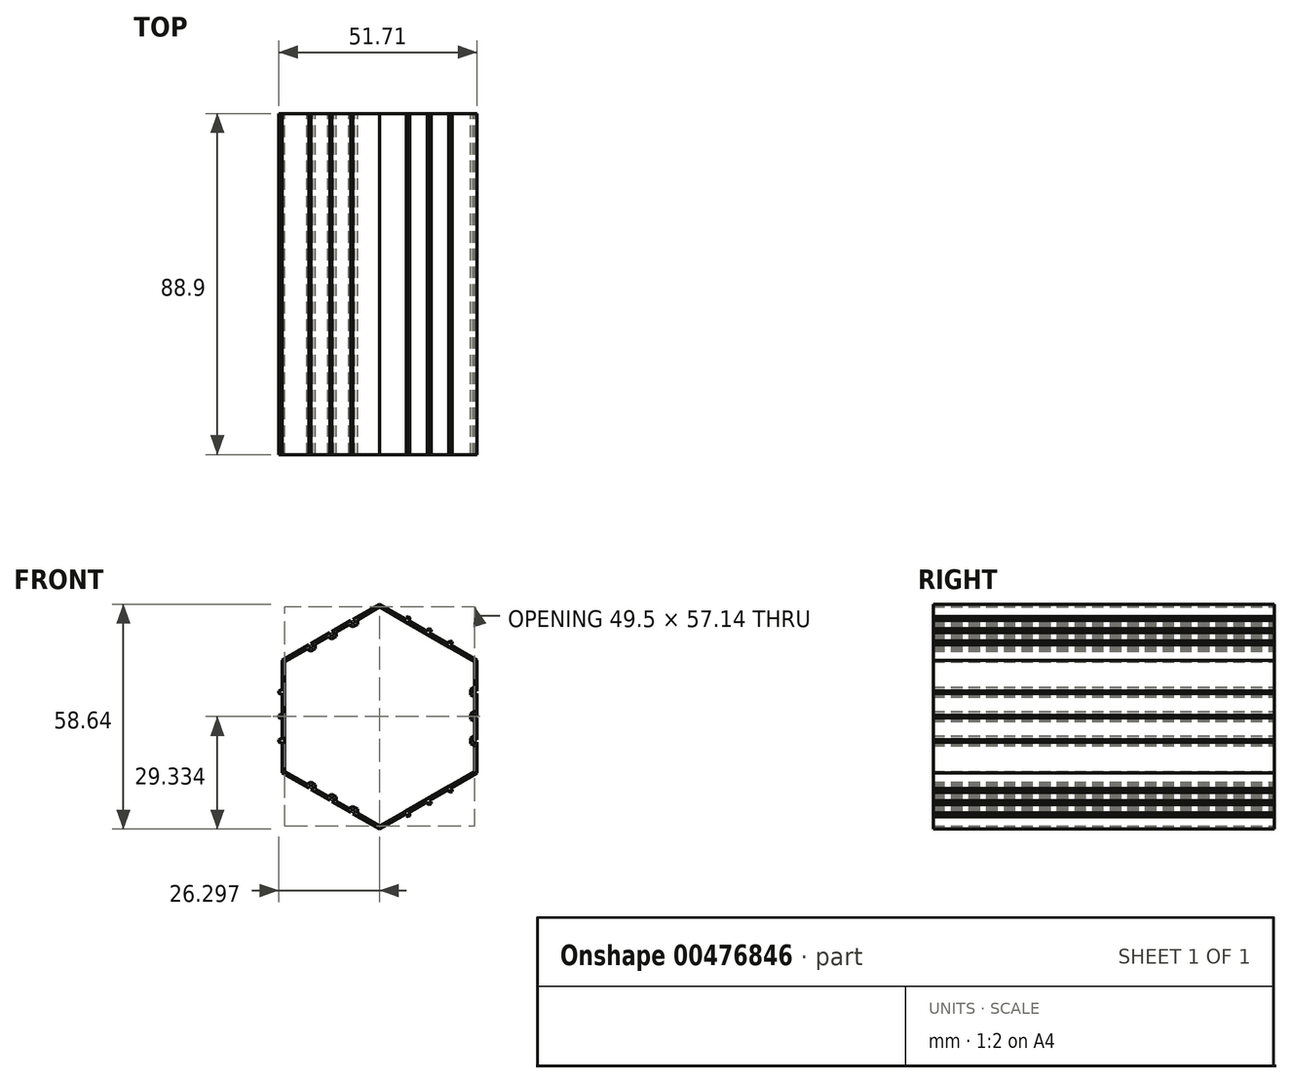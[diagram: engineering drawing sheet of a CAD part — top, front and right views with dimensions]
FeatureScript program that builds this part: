
annotation { "Feature Type Name" : "Feature", "Feature Type Description" : "" }
export const myFeature = defineFeature(function(context is Context, id is Id, definition is map)
    precondition{}
    {
        {
            var Q0;
            Q0=qCreatedBy(makeId("Front.planeOp"),FACE);
            var sketch = newSketch(context, id + "F0", { "sketchPlane" : qUnion([Q0])});
            skLineSegment(sketch, "E0.1", {"start": v(12.47, 22.13) * mm, "end": v(12.47, 22.66) * mm});
            skLineSegment(sketch, "E0.2", {"start": v(12.47, 22.66) * mm, "end": v(12.93, 22.92) * mm});
            skLineSegment(sketch, "E0.3", {"start": v(12.93, 22.92) * mm, "end": v(13.39, 22.66) * mm});
            skLineSegment(sketch, "E0.4", {"start": v(13.39, 22.66) * mm, "end": v(13.39, 22.13) * mm});
            skLineSegment(sketch, "E0.5", {"start": v(13.39, 22.13) * mm, "end": v(12.93, 21.87) * mm});
            skLineSegment(sketch, "E1.MirrorCS", {"start": v(18.43, 19.75) * mm, "end": v(17.97, 19.48) * mm});
            skLineSegment(sketch, "E2.MirrorCS", {"start": v(18.89, 19.48) * mm, "end": v(18.43, 19.75) * mm});
            skLineSegment(sketch, "E3.MirrorCS", {"start": v(18.89, 18.95) * mm, "end": v(18.89, 19.48) * mm});
            skLineSegment(sketch, "E4.MirrorCS", {"start": v(18.43, 18.7) * mm, "end": v(18.89, 18.95) * mm});
            skLineSegment(sketch, "E5.MirrorCS", {"start": v(17.97, 19.48) * mm, "end": v(17.97, 18.95) * mm});
            skLineSegment(sketch, "E6.MirrorCS", {"start": v(7.43, 26.1) * mm, "end": v(6.97, 25.83) * mm});
            skLineSegment(sketch, "E7.MirrorCS", {"start": v(6.97, 25.83) * mm, "end": v(6.98, 25.28) * mm});
            skLineSegment(sketch, "E8.MirrorCS", {"start": v(7.43, 25.04) * mm, "end": v(7.89, 25.3) * mm});
            skLineSegment(sketch, "E9.MirrorCS", {"start": v(7.89, 25.3) * mm, "end": v(7.89, 25.83) * mm});
            skLineSegment(sketch, "E10", {"start": v(7.43, 26.1) * mm, "end": v(7.89, 25.83) * mm});
            skLineSegment(sketch, "E11.MirrorCS", {"start": v(-25.4, -6.61) * mm, "end": v(-25.86, -6.88) * mm});
            skLineSegment(sketch, "E12.MirrorCS", {"start": v(-25.86, -6.88) * mm, "end": v(-26.31, -6.61) * mm});
            skLineSegment(sketch, "E13.MirrorCS", {"start": v(-26.31, -6.61) * mm, "end": v(-26.31, -6.09) * mm});
            skLineSegment(sketch, "E14.MirrorCS", {"start": v(-26.31, -6.09) * mm, "end": v(-25.86, -5.82) * mm});
            skLineSegment(sketch, "E15.MirrorCS", {"start": v(-25.86, -5.82) * mm, "end": v(-25.4, -6.09) * mm});
            skLineSegment(sketch, "E16.MirrorCS", {"start": v(-25.86, -0.53) * mm, "end": v(-25.4, -0.26) * mm});
            skLineSegment(sketch, "E17.MirrorCS", {"start": v(-26.31, -0.26) * mm, "end": v(-25.86, -0.53) * mm});
            skLineSegment(sketch, "E18.MirrorCS", {"start": v(-26.31, 0.26) * mm, "end": v(-26.31, -0.26) * mm});
            skLineSegment(sketch, "E19.MirrorCS", {"start": v(-25.86, 0.53) * mm, "end": v(-26.31, 0.26) * mm});
            skLineSegment(sketch, "E20.MirrorCS", {"start": v(-25.4, 0.26) * mm, "end": v(-25.86, 0.53) * mm});
            skLineSegment(sketch, "E21.MirrorCS", {"start": v(-25.4, 6.09) * mm, "end": v(-25.86, 5.82) * mm});
            skLineSegment(sketch, "E22.MirrorCS", {"start": v(-25.86, 6.88) * mm, "end": v(-25.39, 6.6) * mm});
            skLineSegment(sketch, "E23.MirrorCS", {"start": v(-26.31, 6.61) * mm, "end": v(-25.86, 6.88) * mm});
            skLineSegment(sketch, "E24.MirrorCS", {"start": v(-26.31, 6.61) * mm, "end": v(-26.31, 6.09) * mm});
            skLineSegment(sketch, "E25.MirrorCS", {"start": v(-25.86, 5.82) * mm, "end": v(-26.31, 6.09) * mm});
            skLineSegment(sketch, "E26.MirrorCS", {"start": v(17.97, -18.95) * mm, "end": v(17.97, -19.48) * mm});
            skLineSegment(sketch, "E27.MirrorCS", {"start": v(17.97, -19.48) * mm, "end": v(18.43, -19.75) * mm});
            skLineSegment(sketch, "E28.MirrorCS", {"start": v(18.89, -19.48) * mm, "end": v(18.43, -19.75) * mm});
            skLineSegment(sketch, "E29.MirrorCS", {"start": v(18.89, -19.48) * mm, "end": v(18.89, -18.95) * mm});
            skLineSegment(sketch, "E30.MirrorCS", {"start": v(18.89, -18.95) * mm, "end": v(18.43, -18.7) * mm});
            skLineSegment(sketch, "E31.MirrorCS", {"start": v(12.47, -22.66) * mm, "end": v(12.47, -22.13) * mm});
            skLineSegment(sketch, "E32.MirrorCS", {"start": v(12.93, -22.92) * mm, "end": v(12.47, -22.66) * mm});
            skLineSegment(sketch, "E33.MirrorCS", {"start": v(13.39, -22.66) * mm, "end": v(12.93, -22.92) * mm});
            skLineSegment(sketch, "E34.MirrorCS", {"start": v(13.39, -22.13) * mm, "end": v(13.39, -22.66) * mm});
            skLineSegment(sketch, "E35.MirrorCS", {"start": v(12.93, -21.87) * mm, "end": v(13.39, -22.13) * mm});
            skLineSegment(sketch, "E36.MirrorCS", {"start": v(7.89, -25.3) * mm, "end": v(7.43, -25.04) * mm});
            skLineSegment(sketch, "E37.MirrorCS", {"start": v(7.89, -25.83) * mm, "end": v(7.89, -25.3) * mm});
            skLineSegment(sketch, "E38.MirrorCS", {"start": v(7.43, -26.1) * mm, "end": v(7.89, -25.83) * mm});
            skLineSegment(sketch, "E39.MirrorCS", {"start": v(6.97, -25.83) * mm, "end": v(7.43, -26.1) * mm});
            skLineSegment(sketch, "E40.MirrorCS", {"start": v(6.97, -25.3) * mm, "end": v(6.97, -25.83) * mm});
            skLineSegment(sketch, "E41.2", {"start": v(24.9, -0.59) * mm, "end": v(24.38, -0.3) * mm});
            skLineSegment(sketch, "E41.3", {"start": v(24.38, -0.3) * mm, "end": v(24.38, 0.3) * mm});
            skLineSegment(sketch, "E41.4", {"start": v(24.38, 0.3) * mm, "end": v(24.9, 0.59) * mm});
            skLineSegment(sketch, "E41.5", {"start": v(24.9, 0.59) * mm, "end": v(25.4, 0.3) * mm});
            skLineSegment(sketch, "E42.MirrorCS", {"start": v(25.4, -6.06) * mm, "end": v(24.9, -5.76) * mm});
            skLineSegment(sketch, "E43.MirrorCS", {"start": v(24.9, -5.76) * mm, "end": v(24.38, -6.06) * mm});
            skLineSegment(sketch, "E44.MirrorCS", {"start": v(24.38, -6.06) * mm, "end": v(24.38, -6.64) * mm});
            skLineSegment(sketch, "E45.MirrorCS", {"start": v(24.38, -6.64) * mm, "end": v(24.9, -6.94) * mm});
            skLineSegment(sketch, "E46.MirrorCS", {"start": v(24.9, -6.94) * mm, "end": v(25.4, -6.64) * mm});
            skLineSegment(sketch, "E47.MirrorCS", {"start": v(24.38, 6.06) * mm, "end": v(24.9, 5.76) * mm});
            skLineSegment(sketch, "E48.MirrorCS", {"start": v(24.38, 6.64) * mm, "end": v(24.38, 6.06) * mm});
            skLineSegment(sketch, "E49.MirrorCS", {"start": v(25.4, 6.64) * mm, "end": v(24.9, 6.94) * mm});
            skLineSegment(sketch, "E50.MirrorCS", {"start": v(24.9, 5.76) * mm, "end": v(25.4, 6.06) * mm});
            skLineSegment(sketch, "E51.MirrorCS", {"start": v(24.9, 6.94) * mm, "end": v(24.38, 6.64) * mm});
            skLineSegment(sketch, "E52", {"start": v(24.9, -0.59) * mm, "end": v(25.4, -0.3) * mm});
            skLineSegment(sketch, "E53.MirrorCS", {"start": v(-7.45, -25.03) * mm, "end": v(-7.45, -24.44) * mm});
            skLineSegment(sketch, "E54.MirrorCS", {"start": v(-6.44, -25.03) * mm, "end": v(-6.95, -25.32) * mm});
            skLineSegment(sketch, "E55.MirrorCS", {"start": v(-6.44, -24.44) * mm, "end": v(-6.44, -25.03) * mm});
            skLineSegment(sketch, "E56.MirrorCS", {"start": v(-6.95, -24.15) * mm, "end": v(-6.44, -24.44) * mm});
            skLineSegment(sketch, "E57.MirrorCS", {"start": v(-7.45, -24.44) * mm, "end": v(-6.95, -24.15) * mm});
            skLineSegment(sketch, "E58.MirrorCS", {"start": v(-12.95, -21.26) * mm, "end": v(-12.95, -21.85) * mm});
            skLineSegment(sketch, "E59.MirrorCS", {"start": v(-12.45, -20.97) * mm, "end": v(-12.95, -21.26) * mm});
            skLineSegment(sketch, "E60.MirrorCS", {"start": v(-11.94, -21.26) * mm, "end": v(-12.45, -20.97) * mm});
            skLineSegment(sketch, "E61.MirrorCS", {"start": v(-11.94, -21.85) * mm, "end": v(-11.94, -21.26) * mm});
            skLineSegment(sketch, "E62.MirrorCS", {"start": v(-11.94, -21.85) * mm, "end": v(-12.45, -22.14) * mm});
            skLineSegment(sketch, "E63.MirrorCS", {"start": v(-18.45, -18.68) * mm, "end": v(-18.45, -18.09) * mm});
            skLineSegment(sketch, "E64.MirrorCS", {"start": v(-18.45, -18.09) * mm, "end": v(-17.95, -17.8) * mm});
            skLineSegment(sketch, "E65.MirrorCS", {"start": v(-17.95, -17.8) * mm, "end": v(-17.44, -18.09) * mm});
            skLineSegment(sketch, "E66.MirrorCS", {"start": v(-17.44, -18.09) * mm, "end": v(-17.44, -18.68) * mm});
            skLineSegment(sketch, "E67.MirrorCS", {"start": v(-17.44, -18.68) * mm, "end": v(-17.95, -18.97) * mm});
            skLineSegment(sketch, "E68", {"start": v(0.01, 29.3) * mm, "end": v(6.98, 25.28) * mm});
            skLineSegment(sketch, "E69", {"start": v(7.43, 25.04) * mm, "end": v(12.47, 22.13) * mm});
            skLineSegment(sketch, "E70", {"start": v(12.93, 21.87) * mm, "end": v(17.97, 18.95) * mm});
            skLineSegment(sketch, "E71", {"start": v(18.43, 18.7) * mm, "end": v(25.4, 14.66) * mm});
            skLineSegment(sketch, "E72", {"start": v(25.4, 14.66) * mm, "end": v(25.4, 6.64) * mm});
            skLineSegment(sketch, "E73", {"start": v(25.4, 6.06) * mm, "end": v(25.4, 0.3) * mm});
            skLineSegment(sketch, "E74", {"start": v(25.4, -0.3) * mm, "end": v(25.4, -6.06) * mm});
            skLineSegment(sketch, "E75", {"start": v(25.4, -14.66) * mm, "end": v(25.4, -6.64) * mm});
            skLineSegment(sketch, "E76", {"start": v(25.4, -14.66) * mm, "end": v(18.43, -18.7) * mm});
            skLineSegment(sketch, "E77", {"start": v(17.97, -18.95) * mm, "end": v(12.93, -21.87) * mm});
            skLineSegment(sketch, "E78", {"start": v(12.47, -22.13) * mm, "end": v(7.43, -25.04) * mm});
            skLineSegment(sketch, "E79", {"start": v(6.97, -25.3) * mm, "end": v(0, -29.33) * mm});
            skLineSegment(sketch, "E80", {"start": v(0, -29.33) * mm, "end": v(-6.95, -25.32) * mm});
            skLineSegment(sketch, "E81", {"start": v(-7.45, -25.03) * mm, "end": v(-12.45, -22.14) * mm});
            skLineSegment(sketch, "E82", {"start": v(-12.95, -21.85) * mm, "end": v(-17.95, -18.97) * mm});
            skLineSegment(sketch, "E83", {"start": v(-18.45, -18.68) * mm, "end": v(-25.4, -14.66) * mm});
            skLineSegment(sketch, "E84", {"start": v(-25.39, 14.64) * mm, "end": v(-25.39, 6.6) * mm});
            skLineSegment(sketch, "E85", {"start": v(-25.4, 6.09) * mm, "end": v(-25.4, 0.26) * mm});
            skLineSegment(sketch, "E86", {"start": v(-25.4, -0.26) * mm, "end": v(-25.4, -6.09) * mm});
            skLineSegment(sketch, "E87", {"start": v(-25.4, -6.61) * mm, "end": v(-25.4, -14.66) * mm});
            skLineSegment(sketch, "E88.1", {"start": v(-5.78, 24.06) * mm, "end": v(-5.78, 25.23) * mm});
            skLineSegment(sketch, "E88.2", {"start": v(-6.95, 23.38) * mm, "end": v(-5.78, 24.06) * mm});
            skLineSegment(sketch, "E88.3", {"start": v(-16.78, 17.7) * mm, "end": v(-16.78, 18.88) * mm});
            skLineSegment(sketch, "E88.4", {"start": v(-17.95, 17.03) * mm, "end": v(-16.78, 17.7) * mm});
            skLineSegment(sketch, "E88.5", {"start": v(-18.96, 17.62) * mm, "end": v(-17.95, 17.03) * mm});
            skLineSegment(sketch, "E88.7", {"start": v(-16.78, 18.88) * mm, "end": v(-13.46, 20.8) * mm});
            skLineSegment(sketch, "E88.8", {"start": v(-12.45, 20.2) * mm, "end": v(-13.46, 20.8) * mm});
            skLineSegment(sketch, "E88.9", {"start": v(-11.28, 20.88) * mm, "end": v(-12.45, 20.2) * mm});
            skLineSegment(sketch, "E88.10", {"start": v(-11.28, 22.06) * mm, "end": v(-11.28, 20.88) * mm});
            skLineSegment(sketch, "E88.11", {"start": v(-11.28, 22.06) * mm, "end": v(-7.96, 23.97) * mm});
            skLineSegment(sketch, "E88.12", {"start": v(-7.96, 23.97) * mm, "end": v(-6.95, 23.38) * mm});
            skLineSegment(sketch, "E89.MirrorCS", {"start": v(-18.96, -17.62) * mm, "end": v(-17.95, -17.03) * mm});
            skLineSegment(sketch, "E90.MirrorCS", {"start": v(-17.95, -17.03) * mm, "end": v(-16.78, -17.7) * mm});
            skLineSegment(sketch, "E91.MirrorCS", {"start": v(-16.78, -17.7) * mm, "end": v(-16.78, -18.88) * mm});
            skLineSegment(sketch, "E92.MirrorCS", {"start": v(-16.78, -18.88) * mm, "end": v(-13.46, -20.8) * mm});
            skLineSegment(sketch, "E93.MirrorCS", {"start": v(-12.45, -20.2) * mm, "end": v(-13.46, -20.8) * mm});
            skLineSegment(sketch, "E94.MirrorCS", {"start": v(-11.28, -20.88) * mm, "end": v(-12.45, -20.2) * mm});
            skLineSegment(sketch, "E95.MirrorCS", {"start": v(-11.28, -22.06) * mm, "end": v(-11.28, -20.88) * mm});
            skLineSegment(sketch, "E96.MirrorCS", {"start": v(-11.28, -22.06) * mm, "end": v(-7.96, -23.97) * mm});
            skLineSegment(sketch, "E97.MirrorCS", {"start": v(-7.96, -23.97) * mm, "end": v(-6.95, -23.38) * mm});
            skLineSegment(sketch, "E98.MirrorCS", {"start": v(-6.95, -23.38) * mm, "end": v(-5.78, -24.06) * mm});
            skLineSegment(sketch, "E99.MirrorCS", {"start": v(-5.78, -24.06) * mm, "end": v(-5.78, -25.23) * mm});
            skLineSegment(sketch, "E100.MirrorCS", {"start": v(23.72, -7.02) * mm, "end": v(24.74, -7.61) * mm});
            skLineSegment(sketch, "E101.MirrorCS", {"start": v(23.72, -5.68) * mm, "end": v(23.72, -7.02) * mm});
            skLineSegment(sketch, "E102.MirrorCS", {"start": v(24.74, -5.09) * mm, "end": v(23.72, -5.68) * mm});
            skLineSegment(sketch, "E103.MirrorCS", {"start": v(24.74, -1.26) * mm, "end": v(24.74, -5.09) * mm});
            skLineSegment(sketch, "E104.MirrorCS", {"start": v(24.74, -1.26) * mm, "end": v(23.72, -0.67) * mm});
            skLineSegment(sketch, "E105.MirrorCS", {"start": v(23.72, -0.67) * mm, "end": v(23.72, 0.67) * mm});
            skLineSegment(sketch, "E106.MirrorCS", {"start": v(23.72, 0.67) * mm, "end": v(24.74, 1.26) * mm});
            skLineSegment(sketch, "E107.MirrorCS", {"start": v(24.74, 5.09) * mm, "end": v(24.74, 1.26) * mm});
            skLineSegment(sketch, "E108.MirrorCS", {"start": v(23.72, 5.68) * mm, "end": v(24.74, 5.09) * mm});
            skLineSegment(sketch, "E109.MirrorCS", {"start": v(23.72, 7.02) * mm, "end": v(23.72, 5.68) * mm});
            skLineSegment(sketch, "E110.MirrorCS", {"start": v(24.74, 7.61) * mm, "end": v(23.72, 7.02) * mm});
            skLineSegment(sketch, "E111", {"start": v(6.67, 24.73) * mm, "end": v(18.11, 18.14) * mm});
            skLineSegment(sketch, "E112.MirrorCS", {"start": v(6.67, -24.73) * mm, "end": v(18.11, -18.14) * mm});
            skLineSegment(sketch, "E113", {"start": v(-24.77, -6.61) * mm, "end": v(-24.75, 6.6) * mm});
            skPoint(sketch, "E114", {"position": v(-24.75, 14.28) * mm});
            skLineSegment(sketch, "E115", {"start": v(-24.75, 6.6) * mm, "end": v(-24.75, 14.28) * mm});
            skPoint(sketch, "E116", {"position": v(0.01, 28.57) * mm});
            skLineSegment(sketch, "E117", {"start": v(-5.78, 25.23) * mm, "end": v(0.01, 28.57) * mm});
            skLineSegment(sketch, "E118", {"start": v(6.67, 24.73) * mm, "end": v(0.01, 28.57) * mm});
            skPoint(sketch, "E119", {"position": v(24.74, -14.31) * mm});
            skLineSegment(sketch, "E120", {"start": v(18.11, -18.14) * mm, "end": v(24.74, -14.31) * mm});
            skLineSegment(sketch, "E121", {"start": v(24.74, -7.61) * mm, "end": v(24.74, -14.31) * mm});
            skPoint(sketch, "E122", {"position": v(0, -28.57) * mm});
            skLineSegment(sketch, "E123", {"start": v(-5.78, -25.23) * mm, "end": v(0, -28.57) * mm});
            skLineSegment(sketch, "E124", {"start": v(6.67, -24.73) * mm, "end": v(0, -28.57) * mm});
            skPoint(sketch, "E125", {"position": v(-24.76, -14.27) * mm});
            skLineSegment(sketch, "E126", {"start": v(-24.76, -14.27) * mm, "end": v(-18.96, -17.62) * mm});
            skLineSegment(sketch, "E127", {"start": v(-24.77, -14.27) * mm, "end": v(-24.77, -6.61) * mm});
            skPoint(sketch, "E128", {"position": v(24.74, 14.31) * mm});
            skLineSegment(sketch, "E129", {"start": v(18.11, 18.14) * mm, "end": v(24.74, 14.31) * mm});
            skLineSegment(sketch, "E130", {"start": v(24.74, 14.31) * mm, "end": v(24.74, 7.61) * mm});
            skLineSegment(sketch, "E131", {"start": v(-24.75, 14.28) * mm, "end": v(-18.96, 17.62) * mm});
            skLineSegment(sketch, "E132", {"start": v(-26.31, 0) * mm, "end": v(0, 0) * mm, "construction": true});
            skLineSegment(sketch, "E133.MirrorCS", {"start": v(-17.44, 18.68) * mm, "end": v(-17.95, 18.97) * mm});
            skLineSegment(sketch, "E134.MirrorCS", {"start": v(-18.45, 18.68) * mm, "end": v(-18.45, 18.09) * mm});
            skLineSegment(sketch, "E135.MirrorCS", {"start": v(-18.45, 18.09) * mm, "end": v(-17.95, 17.8) * mm});
            skLineSegment(sketch, "E136.MirrorCS", {"start": v(-17.95, 17.8) * mm, "end": v(-17.44, 18.09) * mm});
            skLineSegment(sketch, "E137.MirrorCS", {"start": v(-17.44, 18.09) * mm, "end": v(-17.44, 18.68) * mm});
            skLineSegment(sketch, "E138.MirrorCS", {"start": v(-11.94, 21.85) * mm, "end": v(-12.45, 22.14) * mm});
            skLineSegment(sketch, "E139.MirrorCS", {"start": v(-11.94, 21.85) * mm, "end": v(-11.94, 21.26) * mm});
            skLineSegment(sketch, "E140.MirrorCS", {"start": v(-11.94, 21.26) * mm, "end": v(-12.45, 20.97) * mm});
            skLineSegment(sketch, "E141.MirrorCS", {"start": v(-12.45, 20.97) * mm, "end": v(-12.95, 21.26) * mm});
            skLineSegment(sketch, "E142.MirrorCS", {"start": v(-12.95, 21.26) * mm, "end": v(-12.95, 21.85) * mm});
            skLineSegment(sketch, "E143.MirrorCS", {"start": v(-6.44, 25.03) * mm, "end": v(-6.95, 25.32) * mm});
            skLineSegment(sketch, "E144.MirrorCS", {"start": v(-6.44, 24.44) * mm, "end": v(-6.44, 25.03) * mm});
            skLineSegment(sketch, "E145.MirrorCS", {"start": v(-6.95, 24.15) * mm, "end": v(-6.44, 24.44) * mm});
            skLineSegment(sketch, "E146.MirrorCS", {"start": v(-7.45, 24.44) * mm, "end": v(-6.95, 24.15) * mm});
            skLineSegment(sketch, "E147.MirrorCS", {"start": v(-7.45, 25.03) * mm, "end": v(-7.45, 24.44) * mm});
            skLineSegment(sketch, "E148", {"start": v(0.01, 29.3) * mm, "end": v(-6.95, 25.32) * mm});
            skLineSegment(sketch, "E149", {"start": v(-7.45, 25.03) * mm, "end": v(-12.45, 22.14) * mm});
            skLineSegment(sketch, "E150", {"start": v(-12.95, 21.85) * mm, "end": v(-17.95, 18.97) * mm});
            skLineSegment(sketch, "E151", {"start": v(-18.45, 18.68) * mm, "end": v(-25.39, 14.64) * mm});
            skSolve(sketch);
        }
        {
            var Q0;
            Q0=makeQuery(id+"F0.imprint","IMPRINT",FACE,{"disambiguationData":[TD([[makeQuery(id+"F0.imprint","IMPRINT",EDGE,{"derivedFrom":sQuery(id+"F0.wireOp",EDGE,"E0.1")}),-1.0]])]});
            extrude(context, id + "F1", {"entities" : qUnion([Q0]), "depth" : 88.9 * mm, "symmetric" : true});
        }
    });
